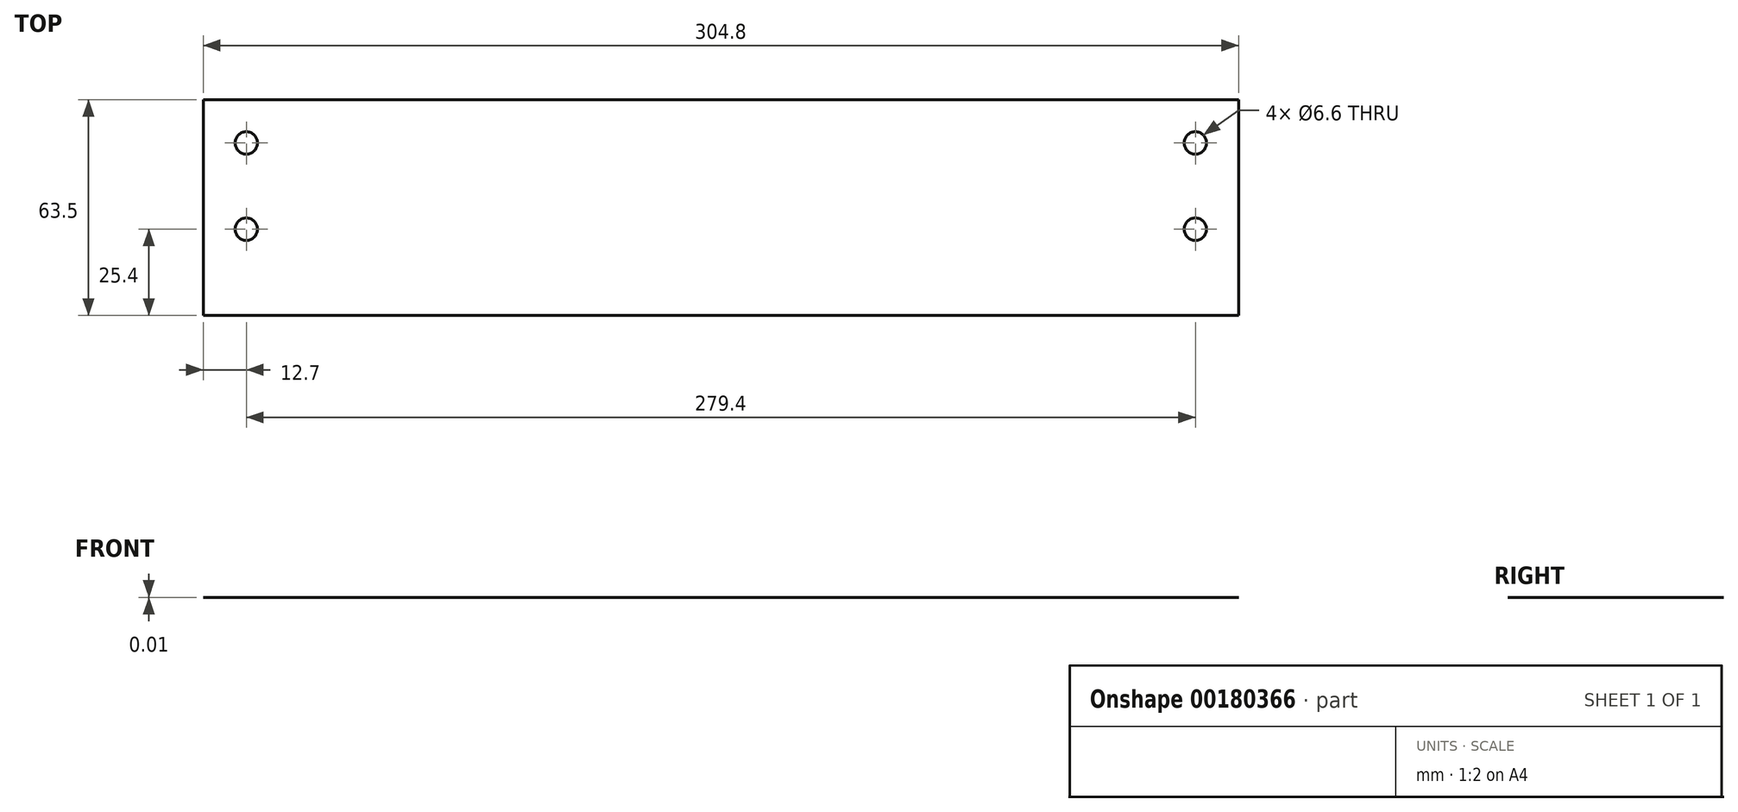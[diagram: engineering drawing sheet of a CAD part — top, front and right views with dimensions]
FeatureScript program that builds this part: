
annotation { "Feature Type Name" : "Feature", "Feature Type Description" : "" }
export const myFeature = defineFeature(function(context is Context, id is Id, definition is map)
    precondition{}
    {
        {
            var Q0;
            Q0=qCreatedBy(makeId("Top.planeOp"),FACE);
            var sketch = newSketch(context, id + "F0", { "sketchPlane" : qUnion([Q0])});
            skLineSegment(sketch, "E0.bottom", {"start": v(152.4, 31.75) * mm, "end": v(-152.4, 31.75) * mm});
            skLineSegment(sketch, "E0.top", {"start": v(152.4, -31.75) * mm, "end": v(-152.4, -31.75) * mm});
            skLineSegment(sketch, "E0.left", {"start": v(152.4, 31.75) * mm, "end": v(152.4, -31.75) * mm});
            skLineSegment(sketch, "E0.right", {"start": v(-152.4, 31.75) * mm, "end": v(-152.4, -31.75) * mm});
            skPoint(sketch, "E0.middle", {"position": v(0, 0) * mm});
            skLineSegment(sketch, "E1", {"start": v(0, 31.75) * mm, "end": v(0, -31.75) * mm, "construction": true});
            skLineSegment(sketch, "E2", {"start": v(-152.4, 0) * mm, "end": v(152.4, 0) * mm, "construction": true});
            skCircle(sketch, "E3", {"center": v(-139.7, 19.05) * mm, "radius": 3.3 * mm});
            skCircle(sketch, "E4", {"center": v(-139.7, -6.35) * mm, "radius": 3.3 * mm});
            skLineSegment(sketch, "E5", {"start": v(-139.7, -6.35) * mm, "end": v(-139.7, 19.05) * mm, "construction": true});
            skCircle(sketch, "E6.MirrorC", {"center": v(139.7, 19.05) * mm, "radius": 3.3 * mm});
            skCircle(sketch, "E7.MirrorC", {"center": v(139.7, -6.35) * mm, "radius": 3.3 * mm});
            skSolve(sketch);
        }
        {
            var Q0;
            Q0=makeQuery(id+"F0.imprint","IMPRINT",FACE,{"disambiguationData":[TD([[makeQuery(id+"F0.imprint","IMPRINT",EDGE,{"derivedFrom":sQuery(id+"F0.wireOp",EDGE,"E0.bottom")}),1.0]])]});
            extrude(context, id + "F1", {"entities" : qUnion([Q0]), "depth" : 3 / 406.4 * mm, "offsetDistance" : 25 * mm});
        }
    });
